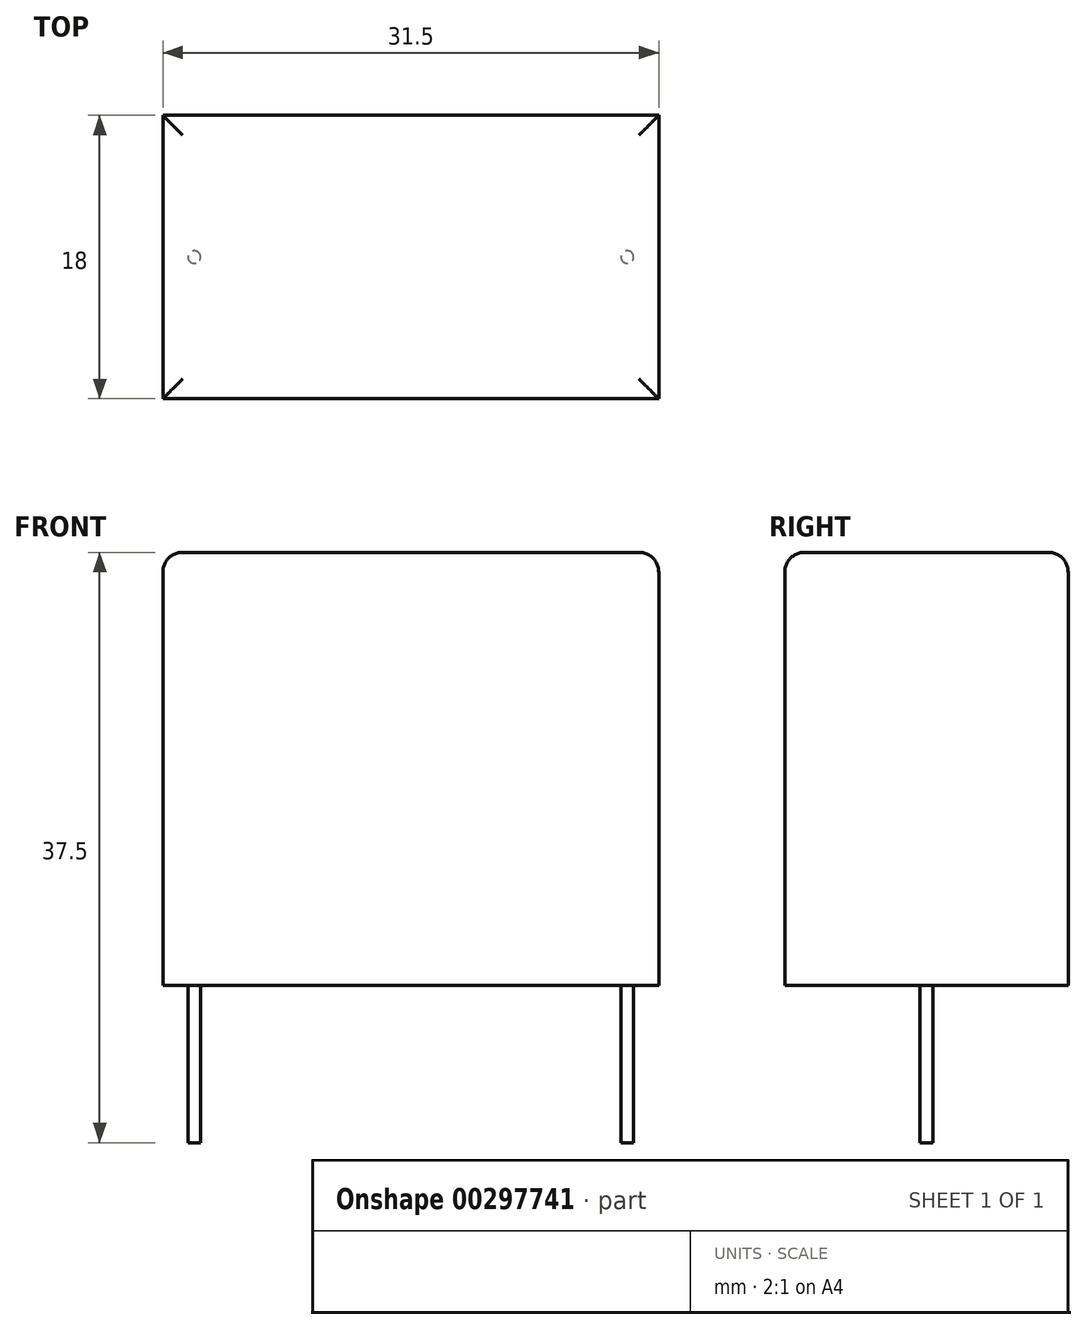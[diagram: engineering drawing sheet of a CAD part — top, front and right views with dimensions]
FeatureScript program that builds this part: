
annotation { "Feature Type Name" : "Feature", "Feature Type Description" : "" }
export const myFeature = defineFeature(function(context is Context, id is Id, definition is map)
    precondition{}
    {
        {
            var Q0;
            Q0=qCreatedBy(makeId("Top.planeOp"),FACE);
            var sketch = newSketch(context, id + "F0", { "sketchPlane" : qUnion([Q0])});
            skLineSegment(sketch, "E0.bottom", {"start": v(15.75, 9) * mm, "end": v(-15.75, 9) * mm});
            skLineSegment(sketch, "E0.top", {"start": v(15.75, -9) * mm, "end": v(-15.75, -9) * mm});
            skLineSegment(sketch, "E0.left", {"start": v(15.75, 9) * mm, "end": v(15.75, -9) * mm});
            skLineSegment(sketch, "E0.right", {"start": v(-15.75, 9) * mm, "end": v(-15.75, -9) * mm});
            skPoint(sketch, "E0.middle", {"position": v(0, 0) * mm});
            skCircle(sketch, "E1", {"center": v(13.75, 0) * mm, "radius": 0.4 * mm});
            skCircle(sketch, "E2", {"center": v(-13.75, 0) * mm, "radius": 0.4 * mm});
            skSolve(sketch);
        }
        {
            var Q0;
            Q0=makeQuery(id+"F0.imprint","IMPRINT",FACE,{"disambiguationData":[TD([[makeQuery(id+"F0.imprint","IMPRINT",EDGE,{"derivedFrom":sQuery(id+"F0.wireOp",EDGE,"E0.bottom")}),1.0]])]});
            var Q1;
            Q1=makeQuery(id+"F0.imprint","IMPRINT",FACE,{"disambiguationData":[TD([[makeQuery(id+"F0.imprint","IMPRINT",EDGE,{"derivedFrom":sQuery(id+"F0.wireOp",EDGE,"E1")}),1.0]])]});
            var Q2;
            Q2=makeQuery(id+"F0.imprint","IMPRINT",FACE,{"disambiguationData":[TD([[makeQuery(id+"F0.imprint","IMPRINT",EDGE,{"derivedFrom":sQuery(id+"F0.wireOp",EDGE,"E2")}),1.0]])]});
            extrude(context, id + "F1", {"entities" : qUnion([Q0, Q1, Q2]), "depth" : 27.5 * mm});
        }
        {
            var Q0;
            Q0=makeQuery(id+"F1.opExtrude","CAP_FACE",FACE,{"disambiguationData":[OSD([sQuery(id+"F0.wireOp",EDGE,"E0.bottom"),sQuery(id+"F0.wireOp",EDGE,"E0.top"),sQuery(id+"F0.wireOp",EDGE,"E0.left"),sQuery(id+"F0.wireOp",EDGE,"E0.right")])],"isStart":true});
            var sketch = newSketch(context, id + "F2", { "sketchPlane" : qUnion([Q0])});
            skCircle(sketch, "E3", {"center": v(13.75, 0) * mm, "radius": 0.4 * mm});
            skCircle(sketch, "E4", {"center": v(-13.75, 0) * mm, "radius": 0.4 * mm});
            skSolve(sketch);
        }
        {
            var Q0;
            Q0 = qSketchRegion(id + "F2", true);
            extrude(context, id + "F3", {"entities" : qUnion([Q0]), "operationType" : NewBodyOperationType.ADD, "depth" : 10 * mm});
        }
        {
            var Q0;
            Q0=makeQuery(id+"F1.opExtrude","CAP_EDGE",EDGE,{"disambiguationData":[OSD([sQuery(id+"F0.wireOp",EDGE,"E0.right")])],"isStart":false});
            var Q1;
            Q1=makeQuery(id+"F1.opExtrude","CAP_EDGE",EDGE,{"disambiguationData":[OSD([sQuery(id+"F0.wireOp",EDGE,"E0.top")])],"isStart":false});
            var Q2;
            Q2=makeQuery(id+"F1.opExtrude","CAP_EDGE",EDGE,{"disambiguationData":[OSD([sQuery(id+"F0.wireOp",EDGE,"E0.left")])],"isStart":false});
            var Q3;
            Q3=makeQuery(id+"F1.opExtrude","CAP_EDGE",EDGE,{"disambiguationData":[OSD([sQuery(id+"F0.wireOp",EDGE,"E0.bottom")])],"isStart":false});
            fillet(context, id + "F4", {"entities" : qUnion([Q0, Q1, Q2, Q3]), "radius" : 1.27 * mm, "tangentPropagation" : true, "allowEdgeOverflow" : false});
        }
    });
